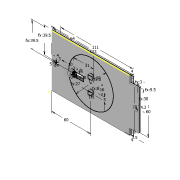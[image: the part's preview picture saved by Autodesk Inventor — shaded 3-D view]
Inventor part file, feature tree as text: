
AUTODESK INVENTOR PART (.ipt)
format: ipt  version: 2022 (Build 260153000, 153)  size: 226,304 bytes
history: native  units: mm
features: extrude x8, sketch x5, fillet x3
ambient origin geometry x8: Origin, YZ Plane, XZ Plane, XY Plane, X Axis, Y Axis, Z Axis, Center Point
bodies: Solid1 (feature_tree)
feature tree (16):
  sketch  "Sketch1"  dims[d0=123.0mm d1=79.0mm]
  extrude  "Extrusion1"  Depth=79.0mm
  extrude  "Extrusion3"  Depth=3.5mm
  sketch  "Sketch2"  dims[d2=111.0mm d3=3.5mm]
  extrude  "Extrusion4"  Depth=60.0mm
  sketch  "Sketch3"  dims[d4=6.0mm d5=60.0mm]
  extrude  "Extrusion5"  Depth=4.0mm
  fillet  "Fillet1"  Radius=4.0mm
  extrude  "Extrusion6"  Depth=3.0mm
  extrude  "Extrusion7"  Depth=1.0mm
  fillet  "Fillet2"  Radius=2.0mm
  extrude  "Extrusion8"  Depth=2.0mm TaperAngle=0.0deg
  fillet  "Fillet3"  Radius=5.0mm
  sketch  "Sketch5"  dims[d9=4.2mm d10=3.0mm d11=30.0mm d12=2.0mm d13=0.0mm d16=2.0mm d17=0.0mm d20=5.0mm d21=3.0mm d22=4.0mm d23=39.5mm d24=68.0mm d25=39.5mm d26=60.0mm d27=16.0mm d28=5.0mm d29=5.0mm d30=8.0mm d31=5.0mm d32=31.0mm d33=27.0mm d34=3.0mm d35=8.0mm d36=64.0mm d37=2.0mm d38=10.0mm d39=3.7mm d40=0.0mm d41=1.1mm d42=1.1mm d43=1.3mm d44=0.0mm d45=0.25mm d46=4.5mm d47=0.0mm d48=2.0mm d49=0.0mm d50=1.0mm d51=16.0mm d52=6.928203mm d53=0.0mm d54=0.0mm d55=1.0mm d56=0.0mm d57=0.0mm]
  extrude  "Extrusion9"  Depth=3.0mm
  sketch  "Sketch4"  dims[d6=9.5mm d7=4.0mm d8=4.0mm]
